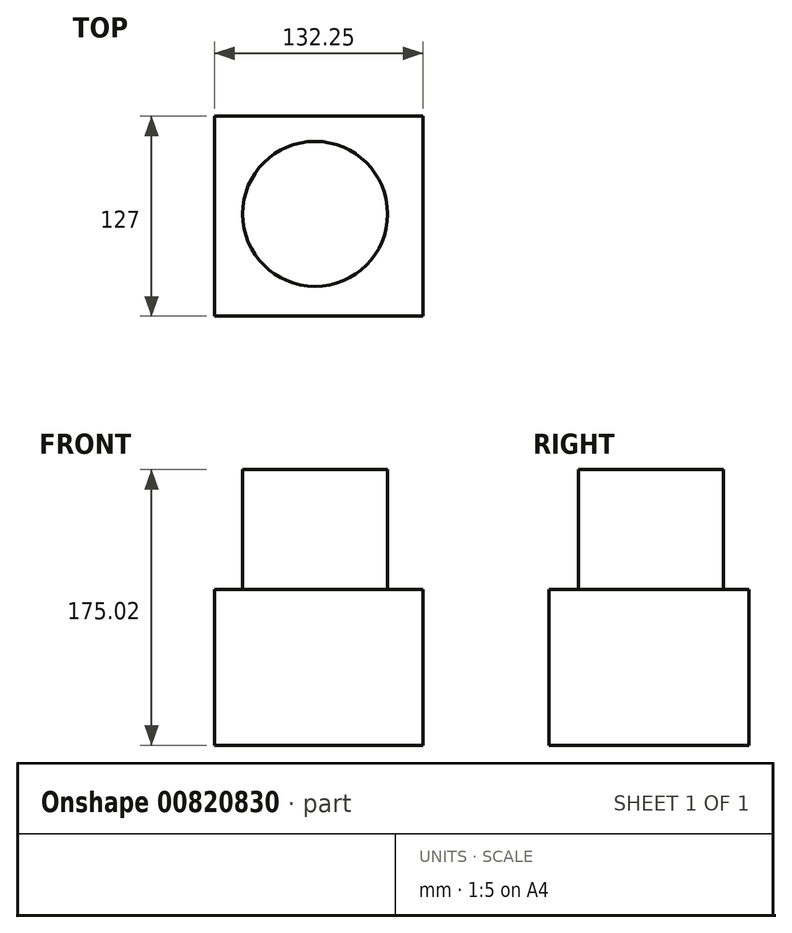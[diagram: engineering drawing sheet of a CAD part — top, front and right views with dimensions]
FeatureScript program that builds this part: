
annotation { "Feature Type Name" : "Feature", "Feature Type Description" : "" }
export const myFeature = defineFeature(function(context is Context, id is Id, definition is map)
    precondition{}
    {
        {
            var Q0;
            Q0=qCreatedBy(makeId("Front.planeOp"),FACE);
            var sketch = newSketch(context, id + "F0", { "sketchPlane" : qUnion([Q0])});
            skLineSegment(sketch, "E0.bottom", {"start": v(-63.79, 45.97) * mm, "end": v(68.46, 45.97) * mm});
            skLineSegment(sketch, "E0.top", {"start": v(-63.79, -52.85) * mm, "end": v(68.46, -52.85) * mm});
            skLineSegment(sketch, "E0.left", {"start": v(-63.79, 45.97) * mm, "end": v(-63.79, -52.85) * mm});
            skLineSegment(sketch, "E0.right", {"start": v(68.46, 45.97) * mm, "end": v(68.46, -52.85) * mm});
            skSolve(sketch);
        }
        {
            var Q0;
            Q0 = qSketchRegion(id + "F0", true);
            extrude(context, id + "F1", {"entities" : qUnion([Q0]), "depth" : 127 * mm, "offsetDistance" : 25.4 * mm});
        }
        {
            var Q0;
            Q0=makeQuery(id+"F1.opExtrude","SWEPT_FACE",FACE,{"disambiguationData":[OSD([sQuery(id+"F0.wireOp",EDGE,"E0.bottom")])]});
            var sketch = newSketch(context, id + "F2", { "sketchPlane" : qUnion([Q0])});
            skCircle(sketch, "E1", {"center": v(0, -62.58) * mm, "radius": 45.92 * mm});
            skSolve(sketch);
        }
        {
            var Q0;
            Q0=makeQuery(id+"F2.imprint","IMPRINT",FACE,{"disambiguationData":[TD([[makeQuery(id+"F2.imprint","IMPRINT",EDGE,{"derivedFrom":sQuery(id+"F2.wireOp",EDGE,"E1")}),1.0]])]});
            var sketch = newSketch(context, id + "F3", { "sketchPlane" : qUnion([Q0])});
            skCircle(sketch, "E2", {"center": v(0, -62.04) * mm, "radius": 46.06 * mm});
            skSolve(sketch);
        }
        {
            var Q0;
            Q0 = qSketchRegion(id + "F3", true);
            extrude(context, id + "F4", {"entities" : qUnion([Q0]), "operationType" : NewBodyOperationType.ADD, "depth" : 76.2 * mm, "offsetDistance" : 25.4 * mm});
        }
    });
